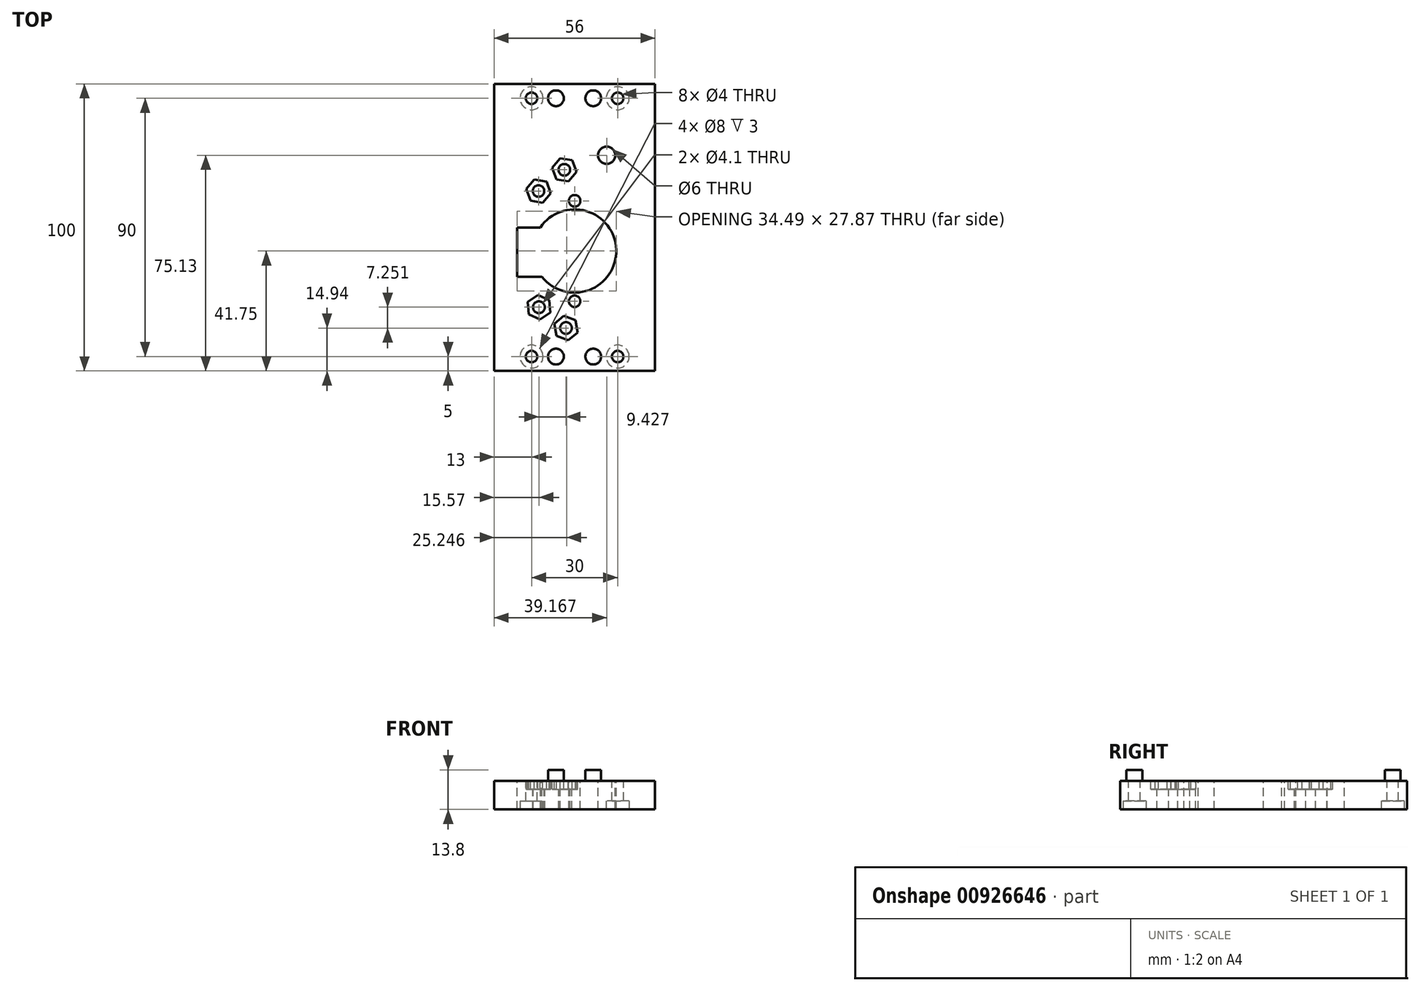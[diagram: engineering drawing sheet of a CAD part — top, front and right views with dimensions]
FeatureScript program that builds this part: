
annotation { "Feature Type Name" : "Feature", "Feature Type Description" : "" }
export const myFeature = defineFeature(function(context is Context, id is Id, definition is map)
    precondition{}
    {
        {
            var Q0;
            Q0=qCreatedBy(makeId("Top.planeOp"),FACE);
            var sketch = newSketch(context, id + "F0", { "sketchPlane" : qUnion([Q0])});
            skLineSegment(sketch, "E0.bottom", {"start": v(0, 0) * mm, "end": v(-28, 0) * mm});
            skLineSegment(sketch, "E0.top", {"start": v(0, 50) * mm, "end": v(-28, 50) * mm});
            skLineSegment(sketch, "E0.left", {"start": v(0, 0) * mm, "end": v(0, 50) * mm});
            skLineSegment(sketch, "E0.right", {"start": v(-28, 0) * mm, "end": v(-28, 50) * mm});
            skSolve(sketch);
        }
        {
            var Q0;
            Q0=makeQuery(id+"F0.imprint","IMPRINT",FACE,{"disambiguationData":[TD([[makeQuery(id+"F0.imprint","IMPRINT",EDGE,{"derivedFrom":sQuery(id+"F0.wireOp",EDGE,"E0.bottom")}),-1.0]])]});
            extrude(context, id + "F1", {"entities" : qUnion([Q0]), "depth" : 10 * mm, "offsetDistance" : 25 * mm});
        }
        {
            var Q0;
            Q0=makeQuery(id+"F1.opExtrude","CAP_FACE",FACE,{"disambiguationData":[OSD([sQuery(id+"F0.wireOp",EDGE,"E0.bottom"),sQuery(id+"F0.wireOp",EDGE,"E0.top"),sQuery(id+"F0.wireOp",EDGE,"E0.left"),sQuery(id+"F0.wireOp",EDGE,"E0.right")])],"isStart":false});
            var sketch = newSketch(context, id + "F2", { "sketchPlane" : qUnion([Q0])});
            skPoint(sketch, "E1", {"position": v(0, 45) * mm});
            skLineSegment(sketch, "E2", {"start": v(0, 45) * mm, "end": v(-28, 45) * mm});
            skPoint(sketch, "E3", {"position": v(-6.5, 45) * mm});
            skPoint(sketch, "E4", {"position": v(-15, 45) * mm});
            skCircle(sketch, "E5", {"center": v(-15, 45) * mm, "radius": 2 * mm});
            skSolve(sketch);
        }
        {
            var Q0;
            Q0 = qSketchRegion(id + "F2", true);
            extrude(context, id + "F3", {"entities" : qUnion([Q0]), "operationType" : NewBodyOperationType.REMOVE, "endBound" : BoundingType.THROUGH_ALL, "oppositeDirection" : true, "depth" : 25 * mm, "offsetDistance" : 25 * mm});
        }
        {
            var Q0;
            Q0=makeQuery(id+"F1.opExtrude","CAP_FACE",FACE,{"disambiguationData":[OSD([sQuery(id+"F0.wireOp",EDGE,"E0.bottom"),sQuery(id+"F0.wireOp",EDGE,"E0.top"),sQuery(id+"F0.wireOp",EDGE,"E0.left"),sQuery(id+"F0.wireOp",EDGE,"E0.right")])],"isStart":false});
            var sketch = newSketch(context, id + "F4", { "sketchPlane" : qUnion([Q0])});
            skLineSegment(sketch, "E6", {"start": v(-15, 45) * mm, "end": v(-6.5, 45) * mm});
            skCircle(sketch, "E7", {"center": v(-6.5, 45) * mm, "radius": 2.75 * mm});
            skSolve(sketch);
        }
        {
            var Q0;
            Q0 = qSketchRegion(id + "F4", true);
            extrude(context, id + "F5", {"entities" : qUnion([Q0]), "operationType" : NewBodyOperationType.ADD, "depth" : 3.8 * mm, "offsetDistance" : 25 * mm});
        }
        {
            var Q0;
            Q0=makeQuery(id+"F1.opExtrude","CAP_FACE",FACE,{"disambiguationData":[OSD([sQuery(id+"F0.wireOp",EDGE,"E0.bottom"),sQuery(id+"F0.wireOp",EDGE,"E0.top"),sQuery(id+"F0.wireOp",EDGE,"E0.left"),sQuery(id+"F0.wireOp",EDGE,"E0.right")])],"isStart":true});
            var sketch = newSketch(context, id + "F6", { "sketchPlane" : qUnion([Q0])});
            skCircle(sketch, "E8", {"center": v(-15, -45) * mm, "radius": 4 * mm});
            skSolve(sketch);
        }
        {
            var Q0;
            Q0 = qSketchRegion(id + "F6", true);
            extrude(context, id + "F7", {"entities" : qUnion([Q0]), "operationType" : NewBodyOperationType.REMOVE, "oppositeDirection" : true, "depth" : 3 * mm, "offsetDistance" : 25 * mm});
        }
        {
            var Q0;
            Q0=makeQuery(id+"F1.opExtrude","SWEPT_BODY",BODY,{"disambiguationData":[OSD([sQuery(id+"F0.wireOp",EDGE,"E0.bottom"),sQuery(id+"F0.wireOp",EDGE,"E0.top"),sQuery(id+"F0.wireOp",EDGE,"E0.left"),sQuery(id+"F0.wireOp",EDGE,"E0.right")])]});
            var Q1;
            Q1=qCreatedBy(makeId("Front.planeOp"),FACE);
            mirror(context, id + "F8", {"operationType" : NewBodyOperationType.ADD, "entities" : qUnion([Q0]), "mirrorPlane" : qUnion([Q1])});
        }
        {
            var Q0;
            Q0=makeQuery(id+"F1.opExtrude","SWEPT_BODY",BODY,{"disambiguationData":[OSD([sQuery(id+"F0.wireOp",EDGE,"E0.bottom"),sQuery(id+"F0.wireOp",EDGE,"E0.top"),sQuery(id+"F0.wireOp",EDGE,"E0.left"),sQuery(id+"F0.wireOp",EDGE,"E0.right")])]});
            var Q1;
            Q1=qCreatedBy(makeId("Right.planeOp"),FACE);
            mirror(context, id + "F9", {"operationType" : NewBodyOperationType.ADD, "entities" : qUnion([Q0]), "mirrorPlane" : qUnion([Q1])});
        }
        {
            var Q0;
            {var subQ0=makeQuery(id+"F1.opExtrude","CAP_FACE",FACE,{"disambiguationData":[OSD([sQuery(id+"F0.wireOp",EDGE,"E0.bottom"),sQuery(id+"F0.wireOp",EDGE,"E0.top"),sQuery(id+"F0.wireOp",EDGE,"E0.left"),sQuery(id+"F0.wireOp",EDGE,"E0.right")])],"isStart":false});var subQ1=makeQuery(id+"F8.boolean.opBoolean","MERGE",FACE,{"derivedFrom":[subQ0,makeQuery(id+"F8.opPattern","COPY",FACE,{"derivedFrom":subQ0,"instanceName":"1"})]});Q0=makeQuery(id+"F9.boolean.opBoolean","MERGE",FACE,{"derivedFrom":[subQ1,makeQuery(id+"F9.opPattern","COPY",FACE,{"derivedFrom":subQ1,"instanceName":"1"})]});}
            var sketch = newSketch(context, id + "F10", { "sketchPlane" : qUnion([Q0])});
            skPoint(sketch, "E9", {"position": v(-28, -40) * mm});
            skLineSegment(sketch, "E10", {"start": v(-28, -40) * mm, "end": v(28, -40) * mm});
            skPoint(sketch, "E11", {"position": v(-18, -50) * mm});
            skLineSegment(sketch, "E12", {"start": v(-18, -50) * mm, "end": v(-18, 50) * mm});
            skPoint(sketch, "E13", {"position": v(18, -50) * mm});
            skLineSegment(sketch, "E14", {"start": v(18, -50) * mm, "end": v(18, 50) * mm});
            skCircle(sketch, "E15", {"center": v(-12.43, -27.8) * mm, "radius": 2.05 * mm});
            skCircle(sketch, "E16", {"center": v(-3, -35.06) * mm, "radius": 2.05 * mm});
            skCircle(sketch, "E17", {"center": v(0, -8.23) * mm, "radius": 14.5 * mm});
            skSolve(sketch);
        }
        {
            var Q0;
            Q0 = qSketchRegion(id + "F10", true);
            extrude(context, id + "F11", {"entities" : qUnion([Q0]), "operationType" : NewBodyOperationType.REMOVE, "endBound" : BoundingType.THROUGH_ALL, "oppositeDirection" : true, "depth" : 25 * mm, "offsetDistance" : 25 * mm});
        }
        {
            var Q0;
            {var subQ0=makeQuery(id+"F1.opExtrude","CAP_FACE",FACE,{"disambiguationData":[OSD([sQuery(id+"F0.wireOp",EDGE,"E0.bottom"),sQuery(id+"F0.wireOp",EDGE,"E0.top"),sQuery(id+"F0.wireOp",EDGE,"E0.left"),sQuery(id+"F0.wireOp",EDGE,"E0.right")])],"isStart":false});var subQ1=makeQuery(id+"F8.boolean.opBoolean","MERGE",FACE,{"derivedFrom":[subQ0,makeQuery(id+"F8.opPattern","COPY",FACE,{"derivedFrom":subQ0,"instanceName":"1"})]});Q0=makeQuery(id+"F9.boolean.opBoolean","MERGE",FACE,{"derivedFrom":[subQ1,makeQuery(id+"F9.opPattern","COPY",FACE,{"derivedFrom":subQ1,"instanceName":"1"})]});}
            var sketch = newSketch(context, id + "F12", { "sketchPlane" : qUnion([Q0])});
            skLineSegment(sketch, "E18.bottom", {"start": v(0, 13.27) * mm, "end": v(0, 13.27) * mm});
            skLineSegment(sketch, "E18.top", {"start": v(0, -29.73) * mm, "end": v(0, -29.73) * mm});
            skLineSegment(sketch, "E18.left", {"start": v(4, 9.27) * mm, "end": v(4, -25.73) * mm});
            skLineSegment(sketch, "E18.right", {"start": v(-4, 9.27) * mm, "end": v(-4, -25.73) * mm});
            skPoint(sketch, "E18.middle", {"position": v(0, -8.23) * mm});
            skPoint(sketch, "E19.visualSharp", {"position": v(-4, -29.73) * mm});
            skArc(sketch, "E19.filletArc", {"start": v(-4, -25.73) * mm, "mid": v(-2.83, -28.56) * mm, "end": v(0, -29.73) * mm});
            skPoint(sketch, "E20.visualSharp", {"position": v(4, -29.73) * mm});
            skArc(sketch, "E20.filletArc", {"start": v(0, -29.73) * mm, "mid": v(2.83, -28.56) * mm, "end": v(4, -25.73) * mm});
            skPoint(sketch, "E21.visualSharp", {"position": v(-4, 13.27) * mm});
            skArc(sketch, "E21.filletArc", {"start": v(0, 13.27) * mm, "mid": v(-2.83, 12.1) * mm, "end": v(-4, 9.27) * mm});
            skPoint(sketch, "E22.visualSharp", {"position": v(4, 13.27) * mm});
            skArc(sketch, "E22.filletArc", {"start": v(4, 9.27) * mm, "mid": v(2.83, 12.1) * mm, "end": v(0, 13.27) * mm});
            skCircle(sketch, "E23", {"center": v(0, -25.73) * mm, "radius": 2 * mm});
            skCircle(sketch, "E24", {"center": v(0, 9.27) * mm, "radius": 2 * mm});
            skSolve(sketch);
        }
        {
            var Q0;
            Q0=makeQuery(id+"F12.imprint","IMPRINT",FACE,{"disambiguationData":[TD([[makeQuery(id+"F12.imprint","IMPRINT",EDGE,{"derivedFrom":sQuery(id+"F12.wireOp",EDGE,"E23")}),1.0]])]});
            var Q1;
            Q1=makeQuery(id+"F12.imprint","IMPRINT",FACE,{"disambiguationData":[TD([[makeQuery(id+"F12.imprint","IMPRINT",EDGE,{"derivedFrom":sQuery(id+"F12.wireOp",EDGE,"E24")}),1.0]])]});
            extrude(context, id + "F13", {"entities" : qUnion([Q0, Q1]), "operationType" : NewBodyOperationType.REMOVE, "endBound" : BoundingType.THROUGH_ALL, "oppositeDirection" : true, "depth" : 25 * mm, "offsetDistance" : 25 * mm});
        }
        {
            var Q0;
            {var subQ0=makeQuery(id+"F1.opExtrude","CAP_FACE",FACE,{"disambiguationData":[OSD([sQuery(id+"F0.wireOp",EDGE,"E0.bottom"),sQuery(id+"F0.wireOp",EDGE,"E0.top"),sQuery(id+"F0.wireOp",EDGE,"E0.left"),sQuery(id+"F0.wireOp",EDGE,"E0.right")])],"isStart":false});var subQ1=makeQuery(id+"F8.boolean.opBoolean","MERGE",FACE,{"derivedFrom":[subQ0,makeQuery(id+"F8.opPattern","COPY",FACE,{"derivedFrom":subQ0,"instanceName":"1"})]});Q0=makeQuery(id+"F9.boolean.opBoolean","MERGE",FACE,{"derivedFrom":[subQ1,makeQuery(id+"F9.opPattern","COPY",FACE,{"derivedFrom":subQ1,"instanceName":"1"})]});}
            var sketch = newSketch(context, id + "F14", { "sketchPlane" : qUnion([Q0])});
            skLineSegment(sketch, "E25", {"start": v(0, -8.23) * mm, "end": v(0, -17.23) * mm});
            skLineSegment(sketch, "E26", {"start": v(0, -17.23) * mm, "end": v(0, 0.77) * mm});
            skLineSegment(sketch, "E27.bottom", {"start": v(0, -17.23) * mm, "end": v(-20, -17.23) * mm});
            skLineSegment(sketch, "E27.top", {"start": v(0, 0) * mm, "end": v(-20, 0) * mm});
            skLineSegment(sketch, "E27.left", {"start": v(0, -17.23) * mm, "end": v(0, 0) * mm});
            skLineSegment(sketch, "E27.right", {"start": v(-20, -17.23) * mm, "end": v(-20, 0) * mm});
            skSolve(sketch);
        }
        {
            var Q0;
            {var subQ0=sQuery(id+"F14.wireOp",EDGE,"E27.right");Q0=makeQuery(id+"F14.imprint","IMPRINT",FACE,{"disambiguationData":[TD([[makeQuery(id+"F14.imprint","IMPRINT",EDGE,{"derivedFrom":subQ0}),-1.0]])]});}
            extrude(context, id + "F15", {"entities" : qUnion([Q0]), "operationType" : NewBodyOperationType.REMOVE, "endBound" : BoundingType.THROUGH_ALL, "oppositeDirection" : true, "depth" : 25 * mm, "offsetDistance" : 25 * mm});
        }
        {
            var Q0;
            {var subQ0=makeQuery(id+"F1.opExtrude","CAP_FACE",FACE,{"disambiguationData":[OSD([sQuery(id+"F0.wireOp",EDGE,"E0.bottom"),sQuery(id+"F0.wireOp",EDGE,"E0.top"),sQuery(id+"F0.wireOp",EDGE,"E0.left"),sQuery(id+"F0.wireOp",EDGE,"E0.right")])],"isStart":false});var subQ1=makeQuery(id+"F8.boolean.opBoolean","MERGE",FACE,{"derivedFrom":[subQ0,makeQuery(id+"F8.opPattern","COPY",FACE,{"derivedFrom":subQ0,"instanceName":"1"})]});Q0=makeQuery(id+"F9.boolean.opBoolean","MERGE",FACE,{"derivedFrom":[subQ1,makeQuery(id+"F9.opPattern","COPY",FACE,{"derivedFrom":subQ1,"instanceName":"1"})]});}
            var sketch = newSketch(context, id + "F16", { "sketchPlane" : qUnion([Q0])});
            skCircle(sketch, "E28", {"center": v(-12.58, 12.69) * mm, "radius": 2 * mm});
            skCircle(sketch, "E29", {"center": v(-3.57, 20.07) * mm, "radius": 2 * mm});
            skPoint(sketch, "E29.first.point", {"position": v(-1.77, 19.2) * mm});
            skPoint(sketch, "E29.second.point", {"position": v(-5.13, 21.32) * mm});
            skPoint(sketch, "E29.third.point", {"position": v(-5.33, 19.11) * mm});
            skCircle(sketch, "E30", {"center": v(-11.75, 30.83) * mm, "radius": 2.9 * mm});
            skSolve(sketch);
        }
        {
            var Q0;
            Q0 = qSketchRegion(id + "F16", true);
            extrude(context, id + "F17", {"entities" : qUnion([Q0]), "operationType" : NewBodyOperationType.REMOVE, "oppositeDirection" : true, "depth" : 25 * mm, "offsetDistance" : 25 * mm});
        }
        {
            var Q0;
            {var subQ0=makeQuery(id+"F1.opExtrude","CAP_FACE",FACE,{"disambiguationData":[OSD([sQuery(id+"F0.wireOp",EDGE,"E0.bottom"),sQuery(id+"F0.wireOp",EDGE,"E0.top"),sQuery(id+"F0.wireOp",EDGE,"E0.left"),sQuery(id+"F0.wireOp",EDGE,"E0.right")])],"isStart":false});var subQ1=makeQuery(id+"F8.boolean.opBoolean","MERGE",FACE,{"derivedFrom":[subQ0,makeQuery(id+"F8.opPattern","COPY",FACE,{"derivedFrom":subQ0,"instanceName":"1"})]});Q0=makeQuery(id+"F9.boolean.opBoolean","MERGE",FACE,{"derivedFrom":[subQ1,makeQuery(id+"F9.opPattern","COPY",FACE,{"derivedFrom":subQ1,"instanceName":"1"})]});}
            var sketch = newSketch(context, id + "F18", { "sketchPlane" : qUnion([Q0])});
            skCircle(sketch, "E31", {"center": v(-12.43, -27.8) * mm, "radius": 3.75 * mm});
            skCircle(sketch, "E32", {"center": v(-3, -35.06) * mm, "radius": 3.75 * mm});
            skCircle(sketch, "E33", {"center": v(-12.58, 12.69) * mm, "radius": 3.75 * mm});
            skCircle(sketch, "E34", {"center": v(-3.57, 20.07) * mm, "radius": 3.75 * mm});
            skCircle(sketch, "E35.cCircle", {"center": v(-12.43, -27.8) * mm, "radius": 3.75 * mm, "construction": true});
            skLineSegment(sketch, "E35.0", {"start": v(-8.51, -29.66) * mm, "end": v(-12.07, -32.12) * mm});
            skLineSegment(sketch, "E35.1", {"start": v(-12.07, -32.12) * mm, "end": v(-15.99, -30.28) * mm});
            skLineSegment(sketch, "E35.2", {"start": v(-15.99, -30.28) * mm, "end": v(-16.35, -25.96) * mm});
            skLineSegment(sketch, "E35.3", {"start": v(-16.35, -25.96) * mm, "end": v(-12.79, -23.5) * mm});
            skLineSegment(sketch, "E35.4", {"start": v(-12.79, -23.5) * mm, "end": v(-8.87, -25.34) * mm});
            skLineSegment(sketch, "E35.5", {"start": v(-8.87, -25.34) * mm, "end": v(-8.51, -29.66) * mm});
            skPoint(sketch, "E35.0.midPoint", {"position": v(-10.3, -30.9) * mm});
            skCircle(sketch, "E36.cCircle", {"center": v(-3, -35.06) * mm, "radius": 3.75 * mm, "construction": true});
            skLineSegment(sketch, "E36.0", {"start": v(-6.35, -37.8) * mm, "end": v(-7.06, -33.53) * mm});
            skLineSegment(sketch, "E36.1", {"start": v(-7.06, -33.53) * mm, "end": v(-3.7, -30.79) * mm});
            skLineSegment(sketch, "E36.2", {"start": v(-3.7, -30.79) * mm, "end": v(0.34, -32.31) * mm});
            skLineSegment(sketch, "E36.3", {"start": v(0.34, -32.31) * mm, "end": v(1.05, -36.59) * mm});
            skLineSegment(sketch, "E36.4", {"start": v(1.05, -36.59) * mm, "end": v(-2.3, -39.33) * mm});
            skLineSegment(sketch, "E36.5", {"start": v(-2.3, -39.33) * mm, "end": v(-6.35, -37.8) * mm});
            skPoint(sketch, "E36.0.midPoint", {"position": v(-6.7, -35.67) * mm});
            skCircle(sketch, "E37.cCircle", {"center": v(-12.58, 12.69) * mm, "radius": 3.75 * mm, "construction": true});
            skLineSegment(sketch, "E37.0", {"start": v(-14.05, 16.76) * mm, "end": v(-9.79, 16) * mm});
            skLineSegment(sketch, "E37.1", {"start": v(-9.79, 16) * mm, "end": v(-8.32, 11.93) * mm});
            skLineSegment(sketch, "E37.2", {"start": v(-8.32, 11.93) * mm, "end": v(-11.1, 8.62) * mm});
            skLineSegment(sketch, "E37.3", {"start": v(-11.1, 8.62) * mm, "end": v(-15.37, 9.38) * mm});
            skLineSegment(sketch, "E37.4", {"start": v(-15.37, 9.38) * mm, "end": v(-16.84, 13.45) * mm});
            skLineSegment(sketch, "E37.5", {"start": v(-16.84, 13.45) * mm, "end": v(-14.05, 16.76) * mm});
            skPoint(sketch, "E37.0.midPoint", {"position": v(-11.92, 16.38) * mm});
            skCircle(sketch, "E38.cCircle", {"center": v(-3.57, 20.07) * mm, "radius": 3.75 * mm, "construction": true});
            skLineSegment(sketch, "E38.0", {"start": v(-6.32, 16.73) * mm, "end": v(-7.84, 20.78) * mm});
            skLineSegment(sketch, "E38.1", {"start": v(-7.84, 20.78) * mm, "end": v(-5.1, 24.13) * mm});
            skLineSegment(sketch, "E38.2", {"start": v(-5.1, 24.13) * mm, "end": v(-0.82, 23.42) * mm});
            skLineSegment(sketch, "E38.3", {"start": v(-0.82, 23.42) * mm, "end": v(0.7, 19.36) * mm});
            skLineSegment(sketch, "E38.4", {"start": v(0.7, 19.36) * mm, "end": v(-2.05, 16.02) * mm});
            skLineSegment(sketch, "E38.5", {"start": v(-2.05, 16.02) * mm, "end": v(-6.32, 16.73) * mm});
            skPoint(sketch, "E38.0.midPoint", {"position": v(-7.08, 18.75) * mm});
            skSolve(sketch);
        }
        {
            var Q0;
            Q0 = qSketchRegion(id + "F18", true);
            extrude(context, id + "F19", {"entities" : qUnion([Q0]), "operationType" : NewBodyOperationType.REMOVE, "oppositeDirection" : true, "depth" : 3 * mm, "offsetDistance" : 25 * mm});
        }
        {
            var Q0;
            {var subQ0=makeQuery(id+"F1.opExtrude","CAP_FACE",FACE,{"disambiguationData":[OSD([sQuery(id+"F0.wireOp",EDGE,"E0.bottom"),sQuery(id+"F0.wireOp",EDGE,"E0.top"),sQuery(id+"F0.wireOp",EDGE,"E0.left"),sQuery(id+"F0.wireOp",EDGE,"E0.right")])],"isStart":false});var subQ1=makeQuery(id+"F8.boolean.opBoolean","MERGE",FACE,{"derivedFrom":[subQ0,makeQuery(id+"F8.opPattern","COPY",FACE,{"derivedFrom":subQ0,"instanceName":"1"})]});Q0=makeQuery(id+"F9.boolean.opBoolean","MERGE",FACE,{"derivedFrom":[subQ1,makeQuery(id+"F9.opPattern","COPY",FACE,{"derivedFrom":subQ1,"instanceName":"1"})]});}
            var sketch = newSketch(context, id + "F20", { "sketchPlane" : qUnion([Q0])});
            skCircle(sketch, "E39", {"center": v(-11.75, 30.83) * mm, "radius": 5.55 * mm});
            skSolve(sketch);
        }
        {
            var Q0;
            Q0 = qSketchRegion(id + "F20", true);
            extrude(context, id + "F21", {"entities" : qUnion([Q0]), "operationType" : NewBodyOperationType.ADD, "oppositeDirection" : true, "depth" : 10 * mm, "offsetDistance" : 25 * mm});
        }
        {
            var Q0;
            {var subQ0=makeQuery(id+"F1.opExtrude","CAP_FACE",FACE,{"disambiguationData":[OSD([sQuery(id+"F0.wireOp",EDGE,"E0.bottom"),sQuery(id+"F0.wireOp",EDGE,"E0.top"),sQuery(id+"F0.wireOp",EDGE,"E0.left"),sQuery(id+"F0.wireOp",EDGE,"E0.right")])],"isStart":false});var subQ1=makeQuery(id+"F8.boolean.opBoolean","MERGE",FACE,{"derivedFrom":[subQ0,makeQuery(id+"F8.opPattern","COPY",FACE,{"derivedFrom":subQ0,"instanceName":"1"})]});Q0=makeQuery(id+"F21.boolean.opBoolean","MERGE",FACE,{"derivedFrom":[makeQuery(id+"F9.boolean.opBoolean","MERGE",FACE,{"derivedFrom":[subQ1,makeQuery(id+"F9.opPattern","COPY",FACE,{"derivedFrom":subQ1,"instanceName":"1"})]}),makeQuery(id+"F21.opExtrude","CAP_FACE",FACE,{"disambiguationData":[OSD([sQuery(id+"F20.wireOp",EDGE,"E39")])],"isStart":true})]});}
            var sketch = newSketch(context, id + "F22", { "sketchPlane" : qUnion([Q0])});
            skCircle(sketch, "E40", {"center": v(11.17, 25.13) * mm, "radius": 3 * mm});
            skSolve(sketch);
        }
        {
            var Q0;
            Q0 = qSketchRegion(id + "F22", true);
            extrude(context, id + "F23", {"entities" : qUnion([Q0]), "operationType" : NewBodyOperationType.REMOVE, "oppositeDirection" : true, "depth" : 25 * mm, "offsetDistance" : 25 * mm});
        }
    });
